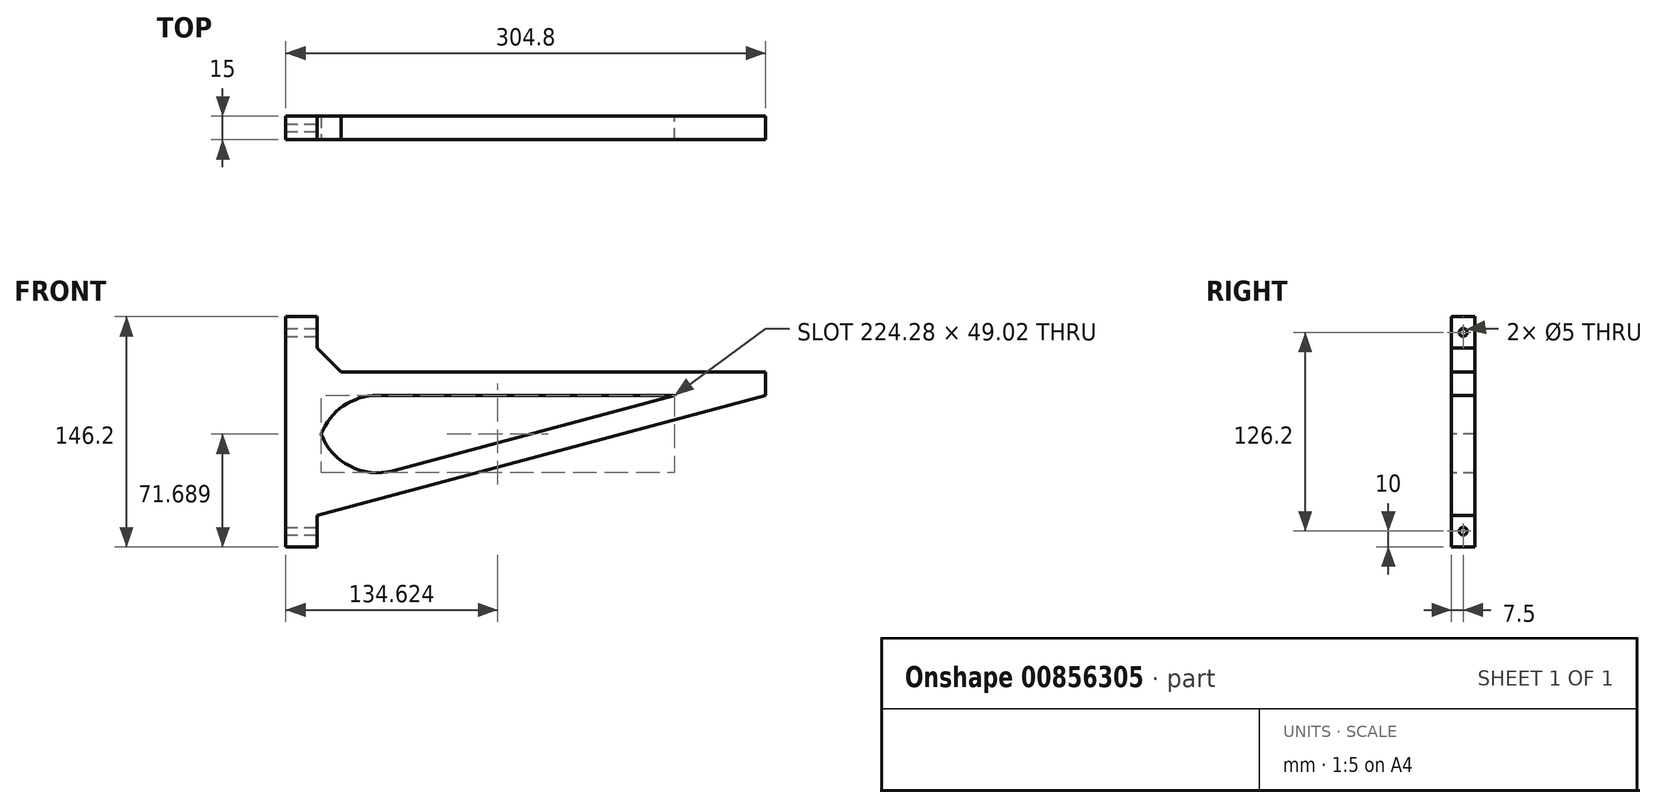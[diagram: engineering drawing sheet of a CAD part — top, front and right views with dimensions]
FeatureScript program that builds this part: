
annotation { "Feature Type Name" : "Feature", "Feature Type Description" : "" }
export const myFeature = defineFeature(function(context is Context, id is Id, definition is map)
    precondition{}
    {
        {
            var Q0;
            Q0=qCreatedBy(makeId("Front.planeOp"),FACE);
            var sketch = newSketch(context, id + "F0", { "sketchPlane" : qUnion([Q0])});
            skLineSegment(sketch, "E0.bottom", {"start": v(0, 0) * mm, "end": v(284.8, 0) * mm});
            skLineSegment(sketch, "E0.top", {"start": v(0, 15) * mm, "end": v(284.8, 15) * mm});
            skLineSegment(sketch, "E0.left", {"start": v(0, 0) * mm, "end": v(0, 15) * mm});
            skLineSegment(sketch, "E0.right", {"start": v(284.8, 0) * mm, "end": v(284.8, 15) * mm});
            skLineSegment(sketch, "E1", {"start": v(284.8, 0) * mm, "end": v(0, -76.2) * mm});
            skLineSegment(sketch, "E2", {"start": v(0, -76.2) * mm, "end": v(0, 0) * mm});
            skLineSegment(sketch, "E3.0", {"start": v(226.77, 0) * mm, "end": v(0, -60.67) * mm});
            skLineSegment(sketch, "E4.bottom", {"start": v(-20, 15) * mm, "end": v(0, 15) * mm});
            skLineSegment(sketch, "E4.top", {"start": v(-20, -76.2) * mm, "end": v(0, -76.2) * mm});
            skLineSegment(sketch, "E4.left", {"start": v(0, 15) * mm, "end": v(0, -76.2) * mm});
            skLineSegment(sketch, "E4.right", {"start": v(-20, 15) * mm, "end": v(-20, -76.2) * mm});
            skLineSegment(sketch, "E5.top", {"start": v(-20, 50) * mm, "end": v(0, 50) * mm});
            skLineSegment(sketch, "E5.left", {"start": v(-20, 15) * mm, "end": v(-20, 50) * mm});
            skLineSegment(sketch, "E5.right", {"start": v(0, 15) * mm, "end": v(0, 50) * mm});
            skSolve(sketch);
        }
        {
            var Q0;
            {var subQ0=makeQuery(id+"F0.imprint","IMPRINT",EDGE,{"derivedFrom":sQuery(id+"F0.wireOp",EDGE,"E4.bottom")});var subQ3=sQuery(id+"F0.wireOp",EDGE,"E1");var subQ7=sQuery(id+"F0.wireOp",EDGE,"E0.left");var subQ10=makeQuery(id+"F0.imprint","IMPRINT",EDGE,{"derivedFrom":subQ7});Q0=qUnion([makeQuery(id+"F0.imprint","IMPRINT",FACE,{"disambiguationData":[TD([[subQ0,1.0]])]}),makeQuery(id+"F0.imprint","IMPRINT",FACE,{"disambiguationData":[TD([[makeQuery(id+"F0.imprint","IMPRINT",EDGE,{"derivedFrom":sQuery(id+"F0.wireOp",EDGE,"E0.top")}),-1.0]])]}),makeQuery(id+"F0.imprint","IMPRINT",FACE,{"disambiguationData":[TD([[makeQuery(id+"F0.imprint","IMPRINT",EDGE,{"derivedFrom":subQ3}),-1.0]])]}),makeQuery(id+"F0.imprint","IMPRINT",FACE,{"disambiguationData":[TD([[subQ10,1.0]])]})]);}
            extrude(context, id + "F1", {"entities" : qUnion([Q0]), "depth" : 15 * mm, "offsetDistance" : 25.4 * mm});
        }
        {
            var Q0;
            Q0=makeQuery(id+"F1.opExtrude","SWEPT_EDGE",EDGE,{"disambiguationData":[OSD([sQuery(id+"F0.wireOp",EDGE,"E0.top"),sQuery(id+"F0.wireOp",EDGE,"E0.left"),sQuery(id+"F0.wireOp",EDGE,"E4.bottom"),sQuery(id+"F0.wireOp",EDGE,"E5.right")])]});
            chamfer(context, id + "F2", {"entities" : qUnion([Q0]), "width" : 15 * mm, "tangentPropagation" : true});
        }
        {
            var Q0;
            Q0=makeQuery(id+"F1.opExtrude","SWEPT_FACE",FACE,{"disambiguationData":[OSD([sQuery(id+"F0.wireOp",EDGE,"E5.right")])]});
            var sketch = newSketch(context, id + "F3", { "sketchPlane" : qUnion([Q0])});
            skLineSegment(sketch, "E6", {"start": v(0, 50) * mm, "end": v(-15, 30) * mm, "construction": true});
            skCircle(sketch, "E7", {"center": v(-7.5, 40) * mm, "radius": 2.5 * mm});
            skSolve(sketch);
        }
        {
            var Q0;
            Q0=makeQuery(id+"F3.imprint","IMPRINT",FACE,{"disambiguationData":[TD([[makeQuery(id+"F3.imprint","IMPRINT",EDGE,{"derivedFrom":sQuery(id+"F3.wireOp",EDGE,"E7")}),1.0]])]});
            extrude(context, id + "F4", {"entities" : qUnion([Q0]), "operationType" : NewBodyOperationType.REMOVE, "endBound" : BoundingType.THROUGH_ALL, "oppositeDirection" : true, "depth" : 25.4 * mm, "offsetDistance" : 25.4 * mm});
        }
        {
            var Q0;
            Q0=makeQuery(id+"F1.opExtrude","SWEPT_FACE",FACE,{"disambiguationData":[OSD([sQuery(id+"F0.wireOp",EDGE,"E4.top")])]});
            var sketch = newSketch(context, id + "F5", { "sketchPlane" : qUnion([Q0])});
            skLineSegment(sketch, "E8.bottom", {"start": v(-20, 15) * mm, "end": v(0, 15) * mm});
            skLineSegment(sketch, "E8.top", {"start": v(-20, 0) * mm, "end": v(0, 0) * mm});
            skLineSegment(sketch, "E8.left", {"start": v(-20, 15) * mm, "end": v(-20, 0) * mm});
            skLineSegment(sketch, "E8.right", {"start": v(0, 15) * mm, "end": v(0, 0) * mm});
            skSolve(sketch);
        }
        {
            var Q0;
            Q0 = qSketchRegion(id + "F5", true);
            extrude(context, id + "F6", {"entities" : qUnion([Q0]), "operationType" : NewBodyOperationType.ADD, "depth" : 20 * mm, "offsetDistance" : 25.4 * mm});
        }
        {
            var Q0;
            Q0=makeQuery(id+"F6.opExtrude","SWEPT_FACE",FACE,{"disambiguationData":[OSD([sQuery(id+"F5.wireOp",EDGE,"E8.right")])]});
            var sketch = newSketch(context, id + "F7", { "sketchPlane" : qUnion([Q0])});
            skLineSegment(sketch, "E9", {"start": v(-15, -76.2) * mm, "end": v(0, -96.2) * mm, "construction": true});
            skCircle(sketch, "E10", {"center": v(-7.5, -86.2) * mm, "radius": 2.5 * mm});
            skSolve(sketch);
        }
        {
            var Q0;
            Q0 = qSketchRegion(id + "F7", true);
            extrude(context, id + "F8", {"entities" : qUnion([Q0]), "operationType" : NewBodyOperationType.REMOVE, "endBound" : BoundingType.THROUGH_ALL, "oppositeDirection" : true, "depth" : 25.4 * mm, "offsetDistance" : 25.4 * mm});
        }
        {
            var Q0;
            Q0=makeQuery(id+"F1.opExtrude","SWEPT_EDGE",EDGE,{"disambiguationData":[OSD([sQuery(id+"F0.wireOp",EDGE,"E2"),sQuery(id+"F0.wireOp",EDGE,"E3.0")])]});
            var Q1;
            Q1=makeQuery(id+"F1.opExtrude","SWEPT_EDGE",EDGE,{"disambiguationData":[OSD([sQuery(id+"F0.wireOp",EDGE,"E0.bottom"),sQuery(id+"F0.wireOp",EDGE,"E0.left"),sQuery(id+"F0.wireOp",EDGE,"E2")])]});
            fillet(context, id + "F9", {"entities" : qUnion([Q0, Q1]), "radius" : 38.1 * mm, "tangentPropagation" : true, "allowEdgeOverflow" : false});
        }
    });
